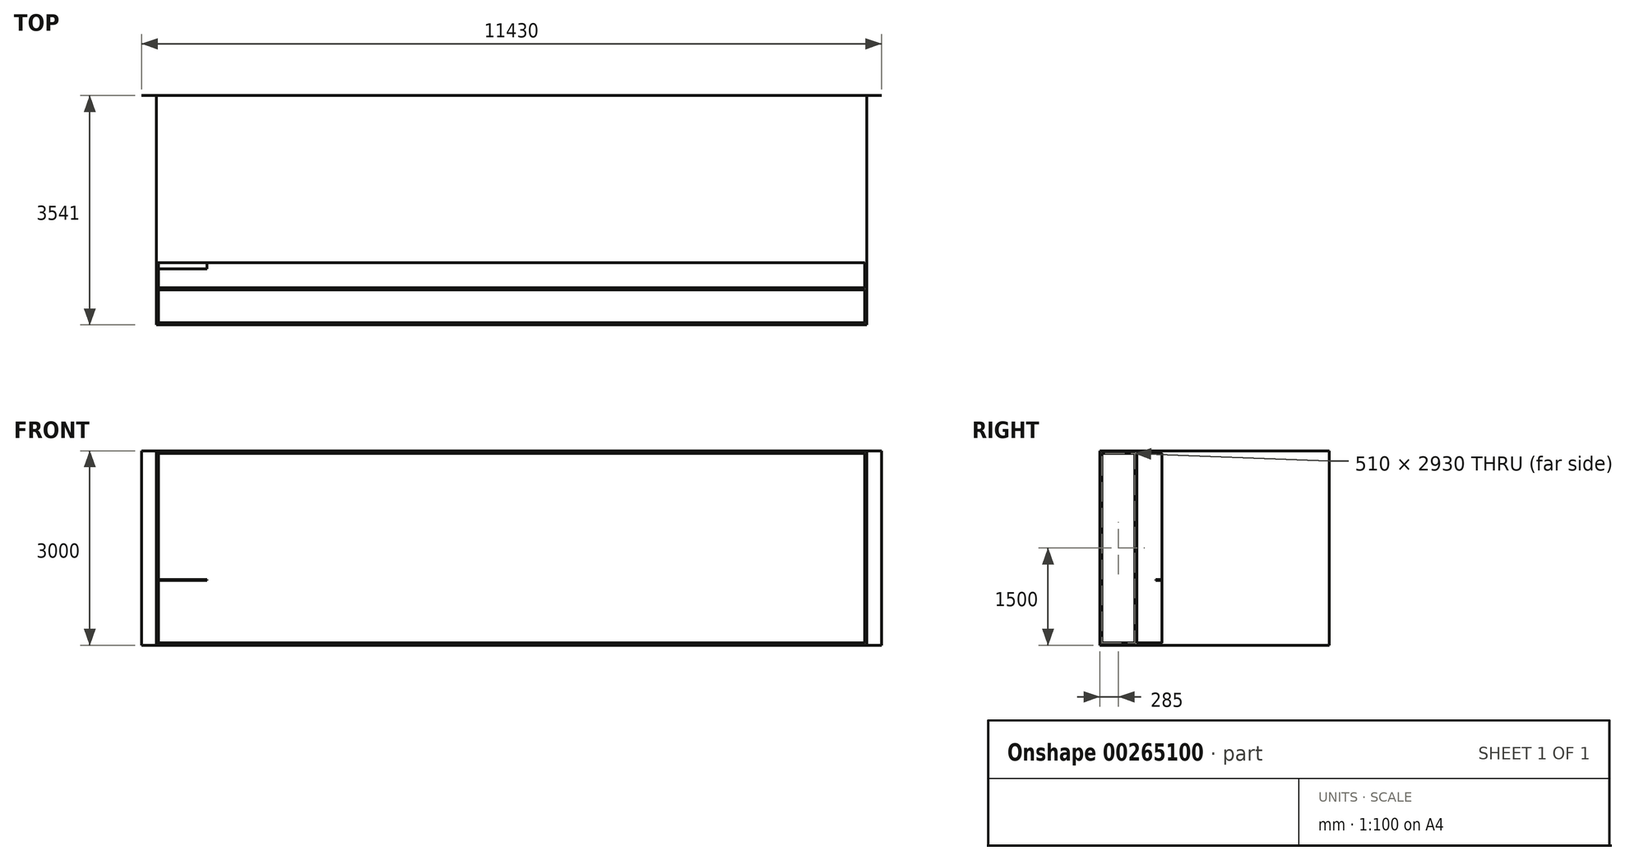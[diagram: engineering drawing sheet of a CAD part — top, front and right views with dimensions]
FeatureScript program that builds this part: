
annotation { "Feature Type Name" : "Feature", "Feature Type Description" : "" }
export const myFeature = defineFeature(function(context is Context, id is Id, definition is map)
    precondition{}
    {
        {
            var Q0;
            Q0=qCreatedBy(makeId("Front.planeOp"),FACE);
            var sketch = newSketch(context, id + "F0", { "sketchPlane" : qUnion([Q0])});
            skLineSegment(sketch, "E0.bottom", {"start": v(-5485, 1500) * mm, "end": v(5485, 1500) * mm});
            skLineSegment(sketch, "E0.top", {"start": v(-5485, -1500) * mm, "end": v(5485, -1500) * mm});
            skLineSegment(sketch, "E0.left", {"start": v(-5485, 1500) * mm, "end": v(-5485, -1500) * mm});
            skLineSegment(sketch, "E0.right", {"start": v(5485, 1500) * mm, "end": v(5485, -1500) * mm});
            skPoint(sketch, "E0.middle", {"position": v(0, 0) * mm});
            skSolve(sketch);
        }
        {
            var Q0;
            Q0 = qSketchRegion(id + "F0", true);
            extrude(context, id + "F1", {"entities" : qUnion([Q0]), "depth" : 2580 * mm});
        }
        {
            var Q0;
            Q0=makeQuery(id+"F1.opExtrude","SWEPT_FACE",FACE,{"disambiguationData":[OSD([sQuery(id+"F0.wireOp",EDGE,"E0.left")])]});
            var sketch = newSketch(context, id + "F2", { "sketchPlane" : qUnion([Q0])});
            skPoint(sketch, "E1.middle", {"position": v(0, 0) * mm});
            skLineSegment(sketch, "E2", {"start": v(2580, 1500) * mm, "end": v(3540, 1500) * mm});
            skLineSegment(sketch, "E3", {"start": v(2580, -1500) * mm, "end": v(3540, -1500) * mm});
            skLineSegment(sketch, "E4", {"start": v(3540, 1500) * mm, "end": v(3540, -1500) * mm});
            skLineSegment(sketch, "E5", {"start": v(3510, 1465) * mm, "end": v(3510, -1465) * mm});
            skLineSegment(sketch, "E6", {"start": v(3540, 1465) * mm, "end": v(3540, -1465) * mm});
            skLineSegment(sketch, "E7", {"start": v(3000, -1465) * mm, "end": v(3000, 1465) * mm});
            skLineSegment(sketch, "E8", {"start": v(2970, 1465) * mm, "end": v(2970, -1465) * mm});
            skLineSegment(sketch, "E9", {"start": v(3510, 1465) * mm, "end": v(2580, 1465) * mm});
            skLineSegment(sketch, "E10", {"start": v(3510, -1465) * mm, "end": v(2580, -1465) * mm});
            skLineSegment(sketch, "E11", {"start": v(2580, 1465) * mm, "end": v(2580, 1500) * mm});
            skLineSegment(sketch, "E12", {"start": v(2580, -1465) * mm, "end": v(2580, -1500) * mm});
            skLineSegment(sketch, "E13", {"start": v(2580, -1500) * mm, "end": v(2580, -500) * mm, "construction": true});
            skLineSegment(sketch, "E14", {"start": v(2580, -500) * mm, "end": v(2679.7, -500) * mm});
            skLineSegment(sketch, "E15", {"start": v(2679.7, -500) * mm, "end": v(2679.7, -487.96) * mm});
            skLineSegment(sketch, "E16", {"start": v(2679.7, -487.96) * mm, "end": v(2580, -487.96) * mm});
            skLineSegment(sketch, "E17", {"start": v(2580, -487.96) * mm, "end": v(2580, -500) * mm});
            skSolve(sketch);
        }
        {
            var Q0;
            {var subQ0=sQuery(id+"F2.wireOp",EDGE,"E4");Q0=makeQuery(id+"F2.imprint","IMPRINT",FACE,{"disambiguationData":[TD([[makeQuery(id+"F2.imprint","IMPRINT",EDGE,{"derivedFrom":subQ0}),-1.0]])]});}
            var Q1;
            {var subQ0=sQuery(id+"F2.wireOp",EDGE,"2suLI4y7-gJnx-pfue-NYUh-xxraCEmb6OIi");Q1=makeQuery(id+"F2.imprint","IMPRINT",FACE,{"disambiguationData":[TD([[makeQuery(id+"F2.imprint","IMPRINT",EDGE,{"derivedFrom":subQ0}),-1.0]])]});}
            var Q2;
            {var subQ0=sQuery(id+"F2.wireOp",EDGE,"E7");Q2=makeQuery(id+"F2.imprint","IMPRINT",FACE,{"disambiguationData":[TD([[makeQuery(id+"F2.imprint","IMPRINT",EDGE,{"derivedFrom":subQ0}),1.0]])]});}
            extrude(context, id + "F3", {"entities" : qUnion([Q0, Q1, Q2]), "oppositeDirection" : true, "depth" : 30 * mm});
        }
        {
            var Q0;
            Q0=makeQuery(id+"F3.opExtrude","CAP_FACE",FACE,{"disambiguationData":[OSD([sQuery(id+"F2.wireOp",EDGE,"E2"),sQuery(id+"F2.wireOp",EDGE,"E3"),sQuery(id+"F2.wireOp",EDGE,"E4"),sQuery(id+"F2.wireOp",EDGE,"E5"),sQuery(id+"F2.wireOp",EDGE,"E6"),sQuery(id+"F2.wireOp",EDGE,"E9"),sQuery(id+"F2.wireOp",EDGE,"E10"),sQuery(id+"F2.wireOp",EDGE,"E11"),sQuery(id+"F2.wireOp",EDGE,"E12")])],"isStart":true});
            var sketch = newSketch(context, id + "F4", { "sketchPlane" : qUnion([Q0])});
            skLineSegment(sketch, "E18.bottom", {"start": v(3000, 1465) * mm, "end": v(2970, 1465) * mm});
            skLineSegment(sketch, "E18.top", {"start": v(3000, 1500) * mm, "end": v(2970, 1500) * mm});
            skLineSegment(sketch, "E18.left", {"start": v(3000, 1465) * mm, "end": v(3000, 1500) * mm});
            skLineSegment(sketch, "E18.right", {"start": v(2970, 1465) * mm, "end": v(2970, 1500) * mm});
            skLineSegment(sketch, "E19.bottom", {"start": v(2970, -1465) * mm, "end": v(3000, -1465) * mm});
            skLineSegment(sketch, "E19.top", {"start": v(2970, -1500) * mm, "end": v(3000, -1500) * mm});
            skLineSegment(sketch, "E19.left", {"start": v(2970, -1465) * mm, "end": v(2970, -1500) * mm});
            skLineSegment(sketch, "E19.right", {"start": v(3000, -1465) * mm, "end": v(3000, -1500) * mm});
            skLineSegment(sketch, "E20.bottom", {"start": v(3540, -1500) * mm, "end": v(3510, -1500) * mm});
            skLineSegment(sketch, "E20.top", {"start": v(3540, -1465) * mm, "end": v(3510, -1465) * mm});
            skLineSegment(sketch, "E20.left", {"start": v(3540, -1500) * mm, "end": v(3540, -1465) * mm});
            skLineSegment(sketch, "E20.right", {"start": v(3510, -1500) * mm, "end": v(3510, -1465) * mm});
            skLineSegment(sketch, "E21.bottom", {"start": v(3510, 1465) * mm, "end": v(3540, 1465) * mm});
            skLineSegment(sketch, "E21.top", {"start": v(3510, 1500) * mm, "end": v(3540, 1500) * mm});
            skLineSegment(sketch, "E21.left", {"start": v(3510, 1465) * mm, "end": v(3510, 1500) * mm});
            skLineSegment(sketch, "E21.right", {"start": v(3540, 1465) * mm, "end": v(3540, 1500) * mm});
            skSolve(sketch);
        }
        {
            var Q0;
            Q0 = qSketchRegion(id + "F4", true);
            extrude(context, id + "F5", {"entities" : qUnion([Q0]), "oppositeDirection" : true, "depth" : 10940 * mm});
        }
        {
            var Q0;
            Q0=makeQuery(id+"F1.opExtrude","SWEPT_FACE",FACE,{"disambiguationData":[OSD([sQuery(id+"F0.wireOp",EDGE,"E0.right")])]});
            var sketch = newSketch(context, id + "F6", { "sketchPlane" : qUnion([Q0])});
            skLineSegment(sketch, "E22", {"start": v(-2580, -1500) * mm, "end": v(-3540, -1500) * mm});
            skLineSegment(sketch, "E23", {"start": v(-3540, -1500) * mm, "end": v(-3540, -1465) * mm});
            skLineSegment(sketch, "E24", {"start": v(-2580, -1465) * mm, "end": v(-2580, 1465) * mm});
            skLineSegment(sketch, "E25", {"start": v(-2580, 1465) * mm, "end": v(-2580, 1500) * mm});
            skLineSegment(sketch, "E26", {"start": v(-2580, 1500) * mm, "end": v(-3540, 1500) * mm});
            skLineSegment(sketch, "E27", {"start": v(-3540, 1500) * mm, "end": v(-3540, 1465) * mm});
            skLineSegment(sketch, "E28", {"start": v(-3510, -1465) * mm, "end": v(-3510, 1465) * mm});
            skLineSegment(sketch, "E29", {"start": v(-3540, 1465) * mm, "end": v(-3540, -1465) * mm});
            skLineSegment(sketch, "E30", {"start": v(-3510, -1465) * mm, "end": v(-3000, -1465) * mm});
            skLineSegment(sketch, "E31", {"start": v(-3000, -1465) * mm, "end": v(-3000, 1465) * mm});
            skLineSegment(sketch, "E32", {"start": v(-2969.84, 1465) * mm, "end": v(-2969.84, -1465) * mm});
            skLineSegment(sketch, "E33", {"start": v(-2969.84, 1465) * mm, "end": v(-2580, 1465) * mm});
            skLineSegment(sketch, "E34", {"start": v(-3510, 1465) * mm, "end": v(-3000, 1465) * mm});
            skLineSegment(sketch, "E35", {"start": v(-2969.84, -1465) * mm, "end": v(-2580, -1465) * mm});
            skSolve(sketch);
        }
        {
            var Q0;
            {var subQ0=sQuery(id+"F6.wireOp",EDGE,"E22");Q0=makeQuery(id+"F6.imprint","IMPRINT",FACE,{"disambiguationData":[TD([[makeQuery(id+"F6.imprint","IMPRINT",EDGE,{"derivedFrom":subQ0}),-1.0]])]});}
            extrude(context, id + "F7", {"entities" : qUnion([Q0]), "operationType" : NewBodyOperationType.ADD, "oppositeDirection" : true, "depth" : 30 * mm});
        }
        {
            var Q0;
            Q0=makeQuery(id+"F1.opExtrude","CAP_FACE",FACE,{"disambiguationData":[OSD([sQuery(id+"F0.wireOp",EDGE,"E0.bottom"),sQuery(id+"F0.wireOp",EDGE,"E0.top"),sQuery(id+"F0.wireOp",EDGE,"E0.left"),sQuery(id+"F0.wireOp",EDGE,"E0.right")])],"isStart":true});
            var sketch = newSketch(context, id + "F8", { "sketchPlane" : qUnion([Q0])});
            skLineSegment(sketch, "E36.bottom", {"start": v(5715, 1500) * mm, "end": v(-5715, 1500) * mm});
            skLineSegment(sketch, "E36.top", {"start": v(5715, -1500) * mm, "end": v(-5715, -1500) * mm});
            skLineSegment(sketch, "E36.left", {"start": v(5715, 1500) * mm, "end": v(5715, -1500) * mm});
            skLineSegment(sketch, "E36.right", {"start": v(-5715, 1500) * mm, "end": v(-5715, -1500) * mm});
            skPoint(sketch, "E36.middle", {"position": v(0, 0) * mm});
            skSolve(sketch);
        }
        {
            var Q0;
            Q0 = qSketchRegion(id + "F8", true);
            extrude(context, id + "F9", {"entities" : qUnion([Q0]), "operationType" : NewBodyOperationType.ADD, "depth" : 1 * mm});
        }
        {
            var Q0;
            Q0=makeQuery(id+"F2.imprint","IMPRINT",FACE,{"disambiguationData":[TD([[makeQuery(id+"F2.imprint","IMPRINT",EDGE,{"derivedFrom":sQuery(id+"F2.wireOp",EDGE,"E14")}),1.0]])]});
            extrude(context, id + "F10", {"entities" : qUnion([Q0]), "operationType" : NewBodyOperationType.ADD, "oppositeDirection" : true, "depth" : 777 * mm});
        }
    });
